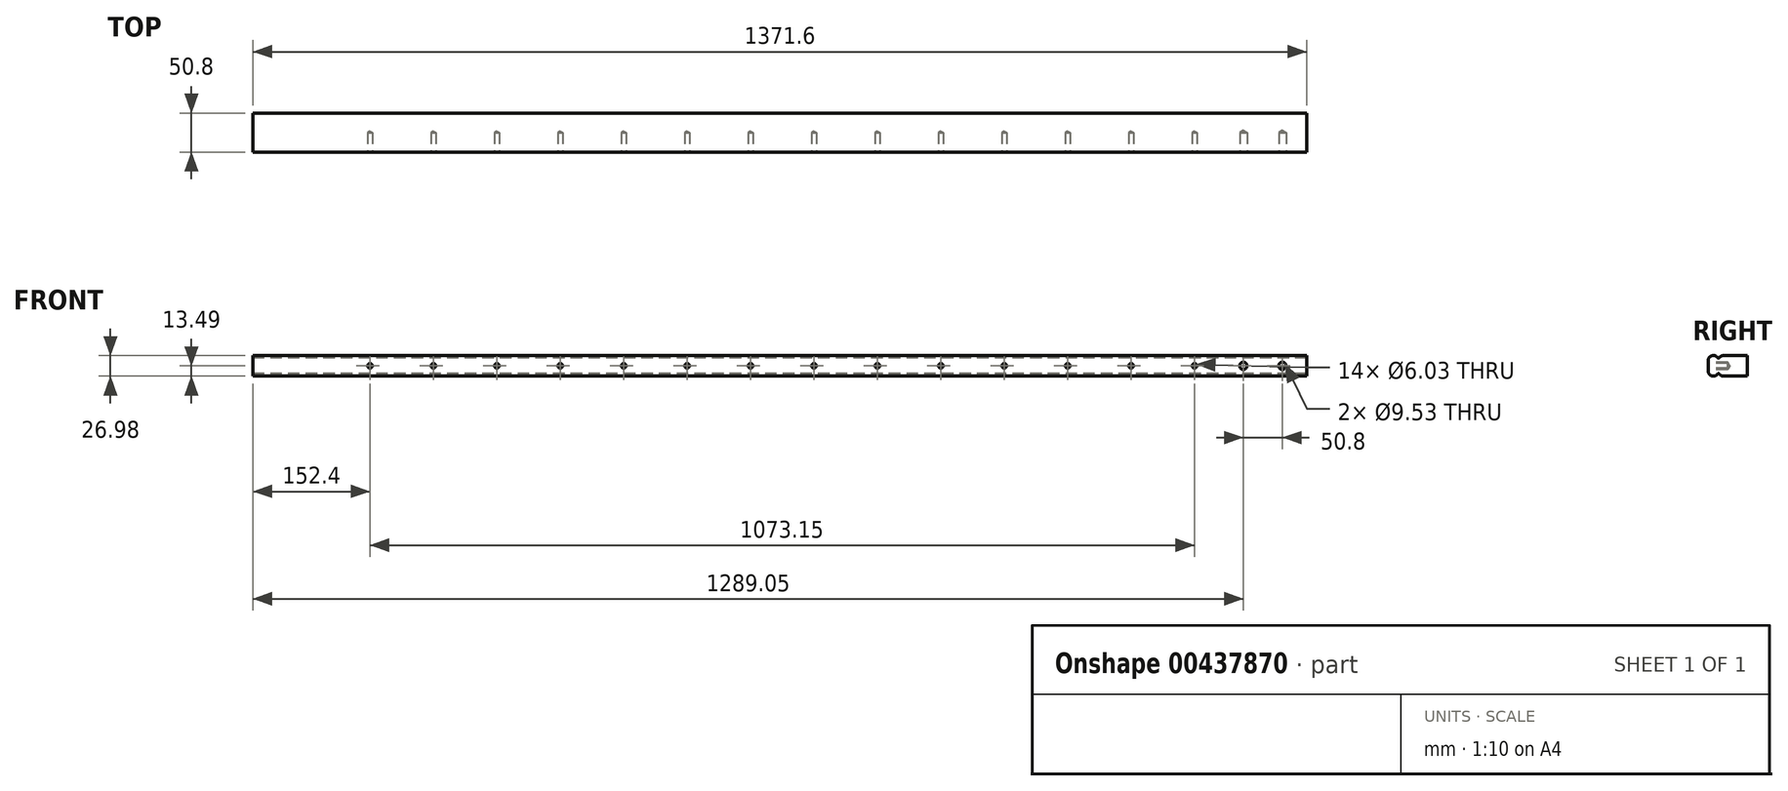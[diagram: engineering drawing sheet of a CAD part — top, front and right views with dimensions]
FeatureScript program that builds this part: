
annotation { "Feature Type Name" : "Feature", "Feature Type Description" : "" }
export const myFeature = defineFeature(function(context is Context, id is Id, definition is map)
    precondition{}
    {
        {
            var Q0;
            Q0=qCreatedBy(makeId("Right.planeOp"),FACE);
            var sketch = newSketch(context, id + "F0", { "sketchPlane" : qUnion([Q0])});
            skLineSegment(sketch, "E0.bottom", {"start": v(25.4, 13.5) * mm, "end": v(-5.16, 13.5) * mm});
            skLineSegment(sketch, "E0.right", {"start": v(-25.4, 6.75) * mm, "end": v(-25.4, -6.75) * mm});
            skArc(sketch, "E1", {"start": v(-13.26, 10.8) * mm, "mid": v(-20.79, 13.15) * mm, "end": v(-25.4, 6.75) * mm});
            skPoint(sketch, "E1.first.point", {"position": v(-25.4, 6.75) * mm});
            skPoint(sketch, "E1.second.point", {"position": v(-18.65, 13.5) * mm});
            skPoint(sketch, "E1.third.point", {"position": v(-18.65, 0) * mm});
            skArc(sketch, "E2", {"start": v(-5.16, 13.5) * mm, "mid": v(-8.18, 12.78) * mm, "end": v(-10.56, 10.8) * mm});
            skPoint(sketch, "E2.first.point", {"position": v(-11.9, 6.75) * mm});
            skPoint(sketch, "E2.second.point", {"position": v(-5.16, 0) * mm});
            skPoint(sketch, "E2.third.point", {"position": v(-5.16, 13.5) * mm});
            skArc(sketch, "E3", {"start": v(-13.26, 10.8) * mm, "mid": v(-11.9, 10.12) * mm, "end": v(-10.56, 10.8) * mm});
            skPoint(sketch, "E3.first.point", {"position": v(-13.26, 10.8) * mm});
            skPoint(sketch, "E3.second.point", {"position": v(-10.56, 10.8) * mm});
            skPoint(sketch, "E3.third.point", {"position": v(-11.9, 13.5) * mm});
            skArc(sketch, "E4.MirrorCS", {"start": v(-13.26, -10.8) * mm, "mid": v(-11.9, -10.12) * mm, "end": v(-10.56, -10.8) * mm});
            skPoint(sketch, "E5.MirrorP", {"position": v(-10.56, -10.8) * mm});
            skPoint(sketch, "E6.MirrorP", {"position": v(-25.4, -6.75) * mm});
            skPoint(sketch, "E7.MirrorP", {"position": v(-13.26, -10.8) * mm});
            skArc(sketch, "E8.MirrorCS", {"start": v(-13.26, -10.8) * mm, "mid": v(-20.79, -13.15) * mm, "end": v(-25.4, -6.75) * mm});
            skPoint(sketch, "E9.MirrorP", {"position": v(-11.9, -13.5) * mm});
            skArc(sketch, "E10.MirrorCS", {"start": v(-5.16, -13.5) * mm, "mid": v(-8.18, -12.78) * mm, "end": v(-10.56, -10.8) * mm});
            skPoint(sketch, "E11.MirrorP", {"position": v(-5.16, -13.5) * mm});
            skPoint(sketch, "E12.MirrorP", {"position": v(-11.9, -6.75) * mm});
            skPoint(sketch, "E13.MirrorP", {"position": v(-18.65, -13.5) * mm});
            skLineSegment(sketch, "E14.MirrorCS", {"start": v(25.4, -13.5) * mm, "end": v(-5.16, -13.5) * mm});
            skLineSegment(sketch, "E15", {"start": v(25.4, 13.5) * mm, "end": v(25.4, -13.5) * mm});
            skSolve(sketch);
        }
        {
            var Q0;
            Q0 = qSketchRegion(id + "F0", true);
            extrude(context, id + "F1", {"entities" : qUnion([Q0]), "depth" : 1371.6 * mm, "symmetric" : true});
        }
        {
            var Q0;
            Q0=makeQuery(id+"F1.opExtrude","SWEPT_FACE",FACE,{"disambiguationData":[OSD([sQuery(id+"F0.wireOp",EDGE,"E0.right")])]});
            var sketch = newSketch(context, id + "F2", { "sketchPlane" : qUnion([Q0])});
            skPoint(sketch, "E16", {"position": v(654.05, 0) * mm});
            skPoint(sketch, "E17", {"position": v(603.25, 0) * mm});
            skSolve(sketch);
        }
        {
            var Q0;
            Q0=sQuery(id+"F2.wireOp",VERTEX,"E16");
            var Q1;
            Q1=sQuery(id+"F2.wireOp",VERTEX,"E17");
            var Q2;
            Q2=makeQuery(id+"F1.opExtrude","SWEPT_BODY",BODY,{"disambiguationData":[OSD([sQuery(id+"F0.wireOp",EDGE,"E0.bottom"),sQuery(id+"F0.wireOp",EDGE,"E0.right"),sQuery(id+"F0.wireOp",EDGE,"E1"),sQuery(id+"F0.wireOp",EDGE,"E2"),sQuery(id+"F0.wireOp",EDGE,"E3"),sQuery(id+"F0.wireOp",EDGE,"E4.MirrorCS"),sQuery(id+"F0.wireOp",EDGE,"E8.MirrorCS"),sQuery(id+"F0.wireOp",EDGE,"E10.MirrorCS"),sQuery(id+"F0.wireOp",EDGE,"E14.MirrorCS"),sQuery(id+"F0.wireOp",EDGE,"E15")])]});
            hole(context, id + "F3", {"style" : HoleStyle.SIMPLE, "endStyle" : HoleEndStyle.BLIND, "holeDiameter" : 9.52 * mm, "holeDepth" : 25.4 * mm, "isTappedThrough" : true, "tappedDepth" : 12.7 * mm, "tapClearance" : 3, "locations" : qUnion([Q0, Q1]), "scope" : qUnion([Q2])});
        }
        {
            var Q0;
            Q0=makeQuery(id+"F1.opExtrude","SWEPT_FACE",FACE,{"disambiguationData":[OSD([sQuery(id+"F0.wireOp",EDGE,"E0.right")])]});
            var sketch = newSketch(context, id + "F4", { "sketchPlane" : qUnion([Q0])});
            skPoint(sketch, "E18", {"position": v(-533.4, 0) * mm});
            skPoint(sketch, "E19.1.0.0", {"position": v(-450.85, 0) * mm});
            skPoint(sketch, "E19.2.0.0", {"position": v(-368.3, 0) * mm});
            skPoint(sketch, "E19.3.0.0", {"position": v(-285.75, 0) * mm});
            skPoint(sketch, "E19.4.0.0", {"position": v(-203.2, 0) * mm});
            skPoint(sketch, "E19.5.0.0", {"position": v(-120.65, 0) * mm});
            skPoint(sketch, "E19.6.0.0", {"position": v(-38.1, 0) * mm});
            skPoint(sketch, "E19.7.0.0", {"position": v(44.45, 0) * mm});
            skPoint(sketch, "E19.8.0.0", {"position": v(127, 0) * mm});
            skPoint(sketch, "E19.9.0.0", {"position": v(209.55, 0) * mm});
            skPoint(sketch, "E19.10.0.0", {"position": v(292.1, 0) * mm});
            skLineSegment(sketch, "E19.direction1", {"start": v(-533.4, 0) * mm, "end": v(-450.85, 0) * mm, "construction": true});
            skPoint(sketch, "E20.0.11.0", {"position": v(374.65, 0) * mm});
            skPoint(sketch, "E21.0.12.0", {"position": v(457.2, 0) * mm});
            skPoint(sketch, "E21.0.13.0", {"position": v(539.75, 0) * mm});
            skSolve(sketch);
        }
        {
            var Q0;
            Q0=sQuery(id+"F4.wireOp",VERTEX,"E18");
            var Q1;
            Q1=sQuery(id+"F4.wireOp",VERTEX,"E19.1.0.0");
            var Q2;
            Q2=sQuery(id+"F4.wireOp",VERTEX,"E19.2.0.0");
            var Q3;
            Q3=sQuery(id+"F4.wireOp",VERTEX,"E19.3.0.0");
            var Q4;
            Q4=sQuery(id+"F4.wireOp",VERTEX,"E19.4.0.0");
            var Q5;
            Q5=sQuery(id+"F4.wireOp",VERTEX,"E19.5.0.0");
            var Q6;
            Q6=sQuery(id+"F4.wireOp",VERTEX,"E19.6.0.0");
            var Q7;
            Q7=sQuery(id+"F4.wireOp",VERTEX,"E19.7.0.0");
            var Q8;
            Q8=sQuery(id+"F4.wireOp",VERTEX,"E19.8.0.0");
            var Q9;
            Q9=sQuery(id+"F4.wireOp",VERTEX,"E19.9.0.0");
            var Q10;
            Q10=sQuery(id+"F4.wireOp",VERTEX,"E19.10.0.0");
            var Q11;
            Q11=sQuery(id+"F4.wireOp",VERTEX,"E20.0.11.0");
            var Q12;
            Q12=sQuery(id+"F4.wireOp",VERTEX,"E21.0.12.0");
            var Q13;
            Q13=sQuery(id+"F4.wireOp",VERTEX,"E21.0.13.0");
            var Q14;
            Q14=makeQuery(id+"F1.opExtrude","SWEPT_BODY",BODY,{"disambiguationData":[OSD([sQuery(id+"F0.wireOp",EDGE,"E0.bottom"),sQuery(id+"F0.wireOp",EDGE,"E0.right"),sQuery(id+"F0.wireOp",EDGE,"E1"),sQuery(id+"F0.wireOp",EDGE,"E2"),sQuery(id+"F0.wireOp",EDGE,"E3"),sQuery(id+"F0.wireOp",EDGE,"E4.MirrorCS"),sQuery(id+"F0.wireOp",EDGE,"E8.MirrorCS"),sQuery(id+"F0.wireOp",EDGE,"E10.MirrorCS"),sQuery(id+"F0.wireOp",EDGE,"E14.MirrorCS"),sQuery(id+"F0.wireOp",EDGE,"E15")])]});
            hole(context, id + "F5", {"style" : HoleStyle.SIMPLE, "endStyle" : HoleEndStyle.BLIND, "holeDiameter" : 6.03 * mm, "holeDepth" : 25.4 * mm, "isTappedThrough" : true, "tappedDepth" : 12.7 * mm, "tapClearance" : 3, "locations" : qUnion([Q0, Q1, Q2, Q3, Q4, Q5, Q6, Q7, Q8, Q9, Q10, Q11, Q12, Q13]), "scope" : qUnion([Q14])});
        }
    });
